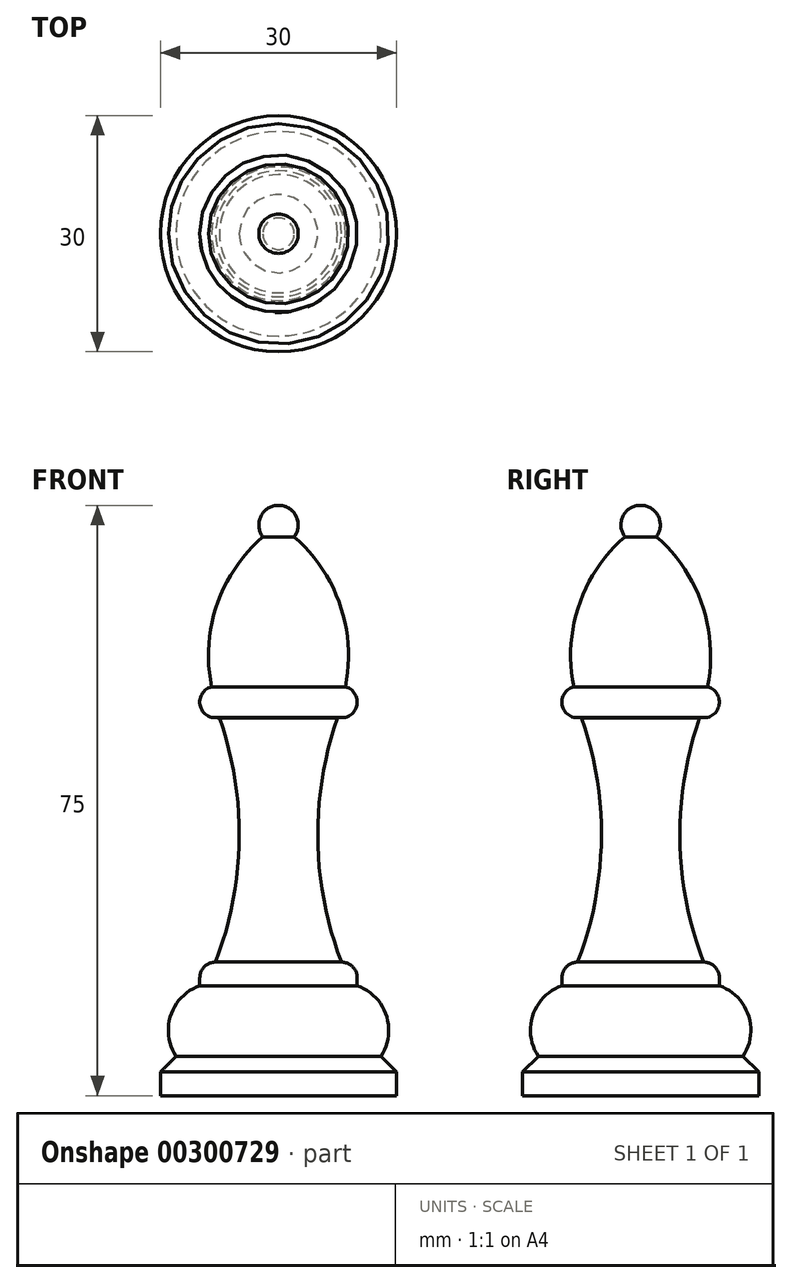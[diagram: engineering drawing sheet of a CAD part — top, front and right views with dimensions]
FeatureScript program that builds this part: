
annotation { "Feature Type Name" : "Feature", "Feature Type Description" : "" }
export const myFeature = defineFeature(function(context is Context, id is Id, definition is map)
    precondition{}
    {
        {
            var Q0;
            Q0=qCreatedBy(makeId("Front.planeOp"),FACE);
            var sketch = newSketch(context, id + "F0", { "sketchPlane" : qUnion([Q0])});
            skArc(sketch, "E0", {"start": v(2, -4) * mm, "mid": v(2.24, -1.38) * mm, "end": v(0, 0) * mm});
            skArc(sketch, "E1", {"start": v(7.5, -27) * mm, "mid": v(5, -42.56) * mm, "end": v(8, -58.03) * mm});
            skArc(sketch, "E2", {"start": v(10, -60.03) * mm, "mid": v(9.41, -58.62) * mm, "end": v(8, -58.03) * mm});
            skLineSegment(sketch, "E3", {"start": v(10, -60.03) * mm, "end": v(10, -61.03) * mm});
            skArc(sketch, "E4", {"start": v(13, -70) * mm, "mid": v(13.69, -64.78) * mm, "end": v(10, -61.03) * mm});
            skLineSegment(sketch, "E5", {"start": v(13, -70) * mm, "end": v(15, -72) * mm});
            skLineSegment(sketch, "E6", {"start": v(15, -72) * mm, "end": v(15, -75) * mm});
            skLineSegment(sketch, "E7", {"start": v(15, -75) * mm, "end": v(0, -75) * mm});
            skLineSegment(sketch, "E8", {"start": v(0, -75) * mm, "end": v(0, 0) * mm});
            skArc(sketch, "E9", {"start": v(8.5, -23.06) * mm, "mid": v(7.82, -12.65) * mm, "end": v(2, -4) * mm});
            skArc(sketch, "E10", {"start": v(8.5, -26.93) * mm, "mid": v(10, -25) * mm, "end": v(8.5, -23.06) * mm});
            skLineSegment(sketch, "E11", {"start": v(8.5, -26.93) * mm, "end": v(7.5, -27) * mm});
            skSolve(sketch);
        }
        {
            var Q0;
            Q0 = qSketchRegion(id + "F0", true);
            var Q1;
            Q1=sQuery(id+"F0.wireOp",EDGE,"E8");
            revolve(context, id + "F1", {"entities" : qUnion([Q0]), "axis" : qUnion([Q1]), "revolveType" : RevolveType.FULL});
        }
    });
